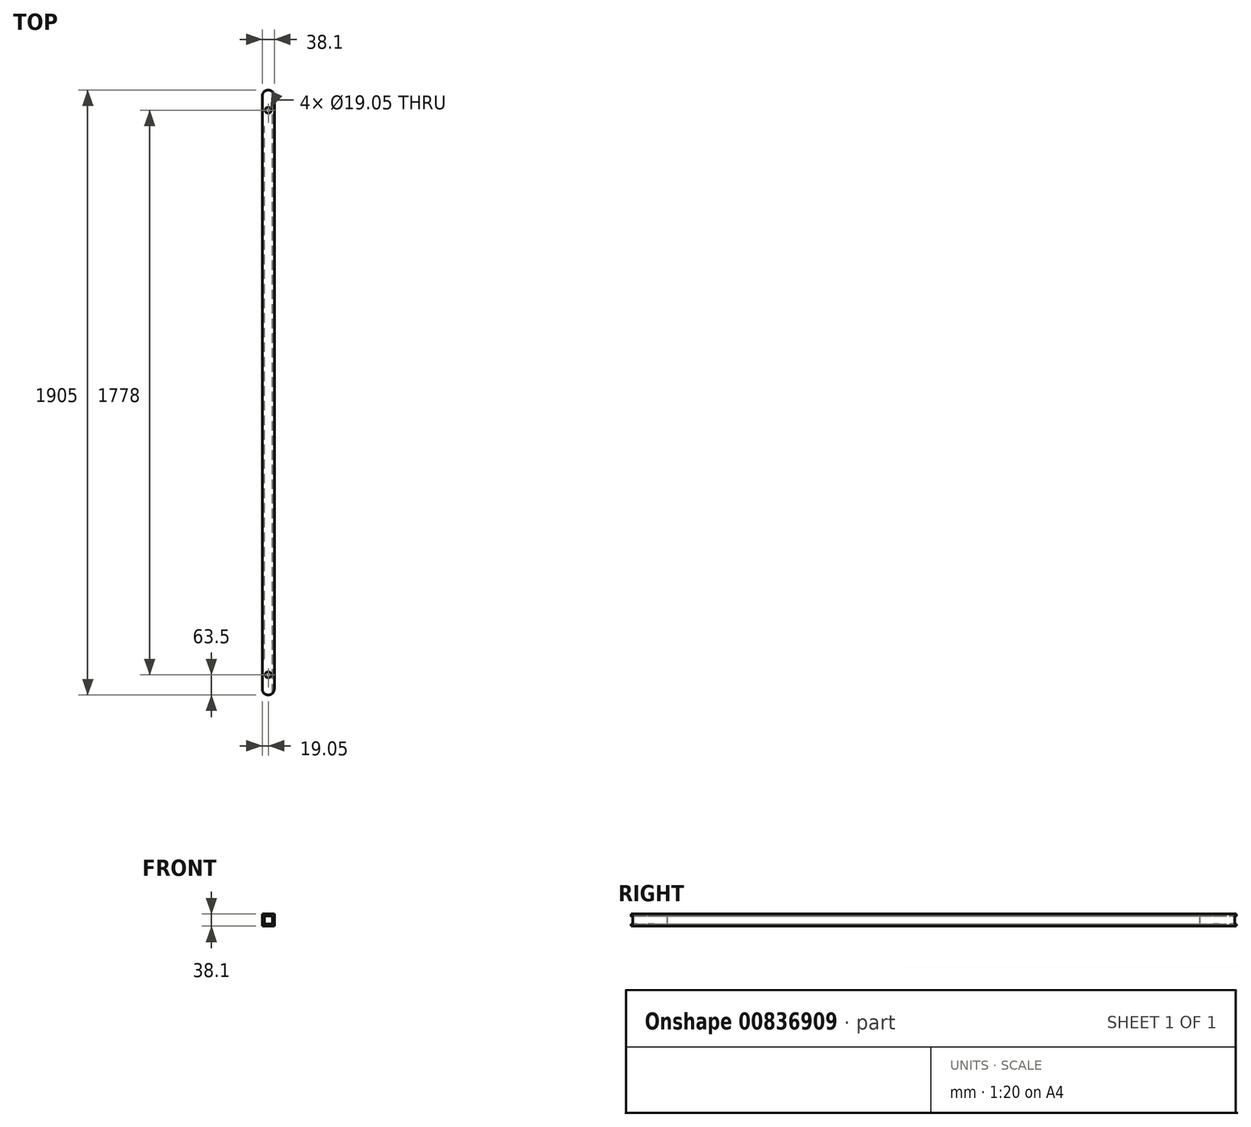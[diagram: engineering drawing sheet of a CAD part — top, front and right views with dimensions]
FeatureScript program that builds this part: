
annotation { "Feature Type Name" : "Feature", "Feature Type Description" : "" }
export const myFeature = defineFeature(function(context is Context, id is Id, definition is map)
    precondition{}
    {
        {
            var Q0;
            Q0=qCreatedBy(makeId("Front.planeOp"),FACE);
            var sketch = newSketch(context, id + "F0", { "sketchPlane" : qUnion([Q0])});
            skLineSegment(sketch, "E0.bottom", {"start": v(19.05, 19.05) * mm, "end": v(-19.05, 19.05) * mm});
            skLineSegment(sketch, "E0.top", {"start": v(19.05, -19.05) * mm, "end": v(-19.05, -19.05) * mm});
            skLineSegment(sketch, "E0.left", {"start": v(19.05, 19.05) * mm, "end": v(19.05, -19.05) * mm});
            skLineSegment(sketch, "E0.right", {"start": v(-19.05, 19.05) * mm, "end": v(-19.05, -19.05) * mm});
            skPoint(sketch, "E0.middle", {"position": v(0, 0) * mm});
            skLineSegment(sketch, "E1.bottom", {"start": v(-12.7, 12.7) * mm, "end": v(12.7, 12.7) * mm});
            skLineSegment(sketch, "E1.top", {"start": v(-12.7, -12.7) * mm, "end": v(12.7, -12.7) * mm});
            skLineSegment(sketch, "E1.left", {"start": v(-12.7, 12.7) * mm, "end": v(-12.7, -12.7) * mm});
            skLineSegment(sketch, "E1.right", {"start": v(12.7, 12.7) * mm, "end": v(12.7, -12.7) * mm});
            skSolve(sketch);
        }
        {
            var Q0;
            Q0 = qSketchRegion(id + "F0", true);
            extrude(context, id + "F1", {"entities" : qUnion([Q0]), "depth" : 1905 * mm, "offsetDistance" : 25.4 * mm, "symmetric" : true});
        }
        {
            var Q0;
            Q0=makeQuery(id+"F1.opExtrude","SWEPT_FACE",FACE,{"disambiguationData":[OSD([sQuery(id+"F0.wireOp",EDGE,"E0.bottom")])]});
            var sketch = newSketch(context, id + "F2", { "sketchPlane" : qUnion([Q0])});
            skCircle(sketch, "E2", {"center": v(0, -889) * mm, "radius": 9.53 * mm});
            skPoint(sketch, "E2.centerSnap0", {"position": v(0, -952.5) * mm});
            skCircle(sketch, "E3", {"center": v(0, 889) * mm, "radius": 9.53 * mm});
            skSolve(sketch);
        }
        {
            var Q0;
            Q0 = qSketchRegion(id + "F2", true);
            extrude(context, id + "F3", {"entities" : qUnion([Q0]), "operationType" : NewBodyOperationType.REMOVE, "oppositeDirection" : true, "depth" : 76.2 * mm, "offsetDistance" : 25.4 * mm});
        }
        {
            var Q0;
            Q0=qCreatedBy(makeId("Right.planeOp"),FACE);
            var sketch = newSketch(context, id + "F4", { "sketchPlane" : qUnion([Q0])});
            skLineSegment(sketch, "E4.bottom", {"start": v(838.2, -12.7) * mm, "end": v(965.2, -12.7) * mm});
            skLineSegment(sketch, "E4.top", {"start": v(838.2, 12.7) * mm, "end": v(965.2, 12.7) * mm});
            skLineSegment(sketch, "E4.left", {"start": v(838.2, -12.7) * mm, "end": v(838.2, 12.7) * mm});
            skLineSegment(sketch, "E4.right", {"start": v(965.2, -12.7) * mm, "end": v(965.2, 12.7) * mm});
            skPoint(sketch, "E4.middle", {"position": v(901.7, 0) * mm});
            skLineSegment(sketch, "E5.bottom", {"start": v(-965.2, -12.7) * mm, "end": v(-838.2, -12.7) * mm});
            skLineSegment(sketch, "E5.top", {"start": v(-965.2, 12.7) * mm, "end": v(-838.2, 12.7) * mm});
            skLineSegment(sketch, "E5.left", {"start": v(-965.2, -12.7) * mm, "end": v(-965.2, 12.7) * mm});
            skLineSegment(sketch, "E5.right", {"start": v(-838.2, -12.7) * mm, "end": v(-838.2, 12.7) * mm});
            skPoint(sketch, "E5.middle", {"position": v(-901.7, 0) * mm});
            skSolve(sketch);
        }
        {
            var Q0;
            Q0 = qSketchRegion(id + "F4", true);
            extrude(context, id + "F5", {"entities" : qUnion([Q0]), "operationType" : NewBodyOperationType.REMOVE, "oppositeDirection" : true, "depth" : 25.4 * mm, "offsetDistance" : 25.4 * mm});
        }
        {
            var Q0;
            Q0=makeQuery(id+"F1.opExtrude","CAP_EDGE",EDGE,{"disambiguationData":[OSD([sQuery(id+"F0.wireOp",EDGE,"E0.left")])],"isStart":false});
            var Q1;
            {var subQ1=sQuery(id+"F0.wireOp",EDGE,"E0.right");var subQ2=sQuery(id+"F0.wireOp",EDGE,"E0.bottom");Q1=makeQuery(id+"F5.boolean.opBoolean","SPLIT",EDGE,{"disambiguationData":[TD([makeQuery(id+"F1.opExtrude","SWEPT_FACE",FACE,{"disambiguationData":[OSD([subQ2])]})])],"derivedFrom":makeQuery(id+"F1.opExtrude","CAP_EDGE",EDGE,{"disambiguationData":[OSD([subQ1])],"isStart":false})});}
            var Q2;
            {var subQ0=sQuery(id+"F0.wireOp",EDGE,"E0.right");var subQ1=sQuery(id+"F0.wireOp",EDGE,"E0.top");Q2=makeQuery(id+"F5.boolean.opBoolean","SPLIT",EDGE,{"disambiguationData":[TD([makeQuery(id+"F1.opExtrude","SWEPT_FACE",FACE,{"disambiguationData":[OSD([subQ1])]})])],"derivedFrom":makeQuery(id+"F1.opExtrude","CAP_EDGE",EDGE,{"disambiguationData":[OSD([subQ0])],"isStart":false})});}
            var Q3;
            Q3=makeQuery(id+"F1.opExtrude","CAP_EDGE",EDGE,{"disambiguationData":[OSD([sQuery(id+"F0.wireOp",EDGE,"E0.left")])],"isStart":true});
            var Q4;
            {var subQ1=sQuery(id+"F0.wireOp",EDGE,"E0.right");var subQ2=sQuery(id+"F0.wireOp",EDGE,"E0.bottom");Q4=makeQuery(id+"F5.boolean.opBoolean","SPLIT",EDGE,{"disambiguationData":[TD([makeQuery(id+"F1.opExtrude","SWEPT_FACE",FACE,{"disambiguationData":[OSD([subQ2])]})])],"derivedFrom":makeQuery(id+"F1.opExtrude","CAP_EDGE",EDGE,{"disambiguationData":[OSD([subQ1])],"isStart":true})});}
            var Q5;
            {var subQ1=sQuery(id+"F0.wireOp",EDGE,"E0.right");var subQ2=sQuery(id+"F0.wireOp",EDGE,"E0.top");Q5=makeQuery(id+"F5.boolean.opBoolean","SPLIT",EDGE,{"disambiguationData":[TD([makeQuery(id+"F1.opExtrude","SWEPT_FACE",FACE,{"disambiguationData":[OSD([subQ2])]})])],"derivedFrom":makeQuery(id+"F1.opExtrude","CAP_EDGE",EDGE,{"disambiguationData":[OSD([subQ1])],"isStart":true})});}
            fillet(context, id + "F6", {"entities" : qUnion([Q0, Q1, Q2, Q3, Q4, Q5]), "radius" : 19.05 * mm, "tangentPropagation" : true, "allowEdgeOverflow" : false});
        }
    });
